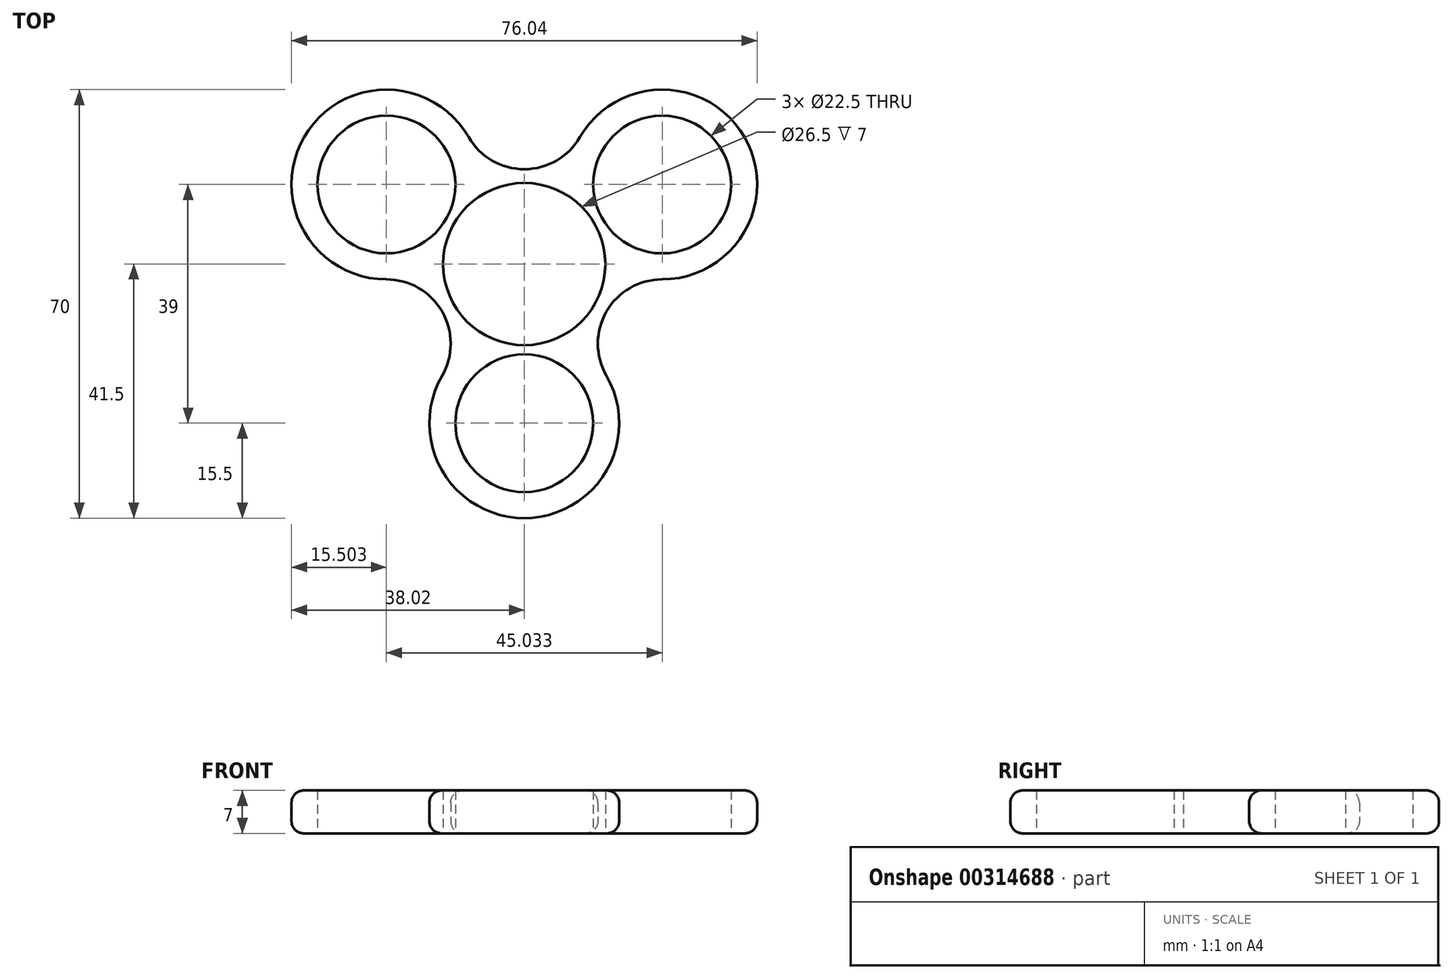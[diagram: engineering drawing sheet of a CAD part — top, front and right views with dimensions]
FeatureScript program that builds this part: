
annotation { "Feature Type Name" : "Feature", "Feature Type Description" : "" }
export const myFeature = defineFeature(function(context is Context, id is Id, definition is map)
    precondition{}
    {
        {
            var Q0;
            Q0=qCreatedBy(makeId("Top.planeOp"),FACE);
            var sketch = newSketch(context, id + "F0", { "sketchPlane" : qUnion([Q0])});
            skCircle(sketch, "E0", {"center": v(0, 0) * mm, "radius": 26 * mm, "construction": true});
            skCircle(sketch, "E1", {"center": v(0, 0) * mm, "radius": 13.25 * mm});
            skLineSegment(sketch, "E2", {"start": v(0, 35.35) * mm, "end": v(0, -50.13) * mm, "construction": true});
            skLineSegment(sketch, "E3", {"start": v(38.37, 22.15) * mm, "end": v(-45.13, -26.05) * mm, "construction": true});
            skLineSegment(sketch, "E4", {"start": v(-44.11, 25.47) * mm, "end": v(51.32, -29.63) * mm, "construction": true});
            skCircle(sketch, "E5", {"center": v(0, -26) * mm, "radius": 11.25 * mm});
            skCircle(sketch, "E6", {"center": v(-22.52, 13) * mm, "radius": 11.25 * mm});
            skCircle(sketch, "E7", {"center": v(22.52, 13) * mm, "radius": 11.25 * mm});
            skCircle(sketch, "E8", {"center": v(-22.52, 13) * mm, "radius": 15.5 * mm});
            skCircle(sketch, "E9", {"center": v(0, -26) * mm, "radius": 15.5 * mm});
            skCircle(sketch, "E10", {"center": v(22.52, 13) * mm, "radius": 15.5 * mm});
            skCircle(sketch, "E11", {"center": v(0, 26) * mm, "radius": 10.5 * mm});
            skCircle(sketch, "E12", {"center": v(22.52, -13) * mm, "radius": 10.5 * mm});
            skCircle(sketch, "E13", {"center": v(-22.52, -13) * mm, "radius": 10.5 * mm});
            skCircle(sketch, "E14", {"center": v(0, 0) * mm, "radius": 17.5 * mm});
            skCircle(sketch, "E15", {"center": v(0, 0) * mm, "radius": 41.5 * mm, "construction": true});
            skSolve(sketch);
        }
        {
            var Q0;
            Q0=makeQuery(id+"F0.imprint","IMPRINT",FACE,{"disambiguationData":[TD([[makeQuery(id+"F0.imprint","IMPRINT",EDGE,{"derivedFrom":sQuery(id+"F0.wireOp",EDGE,"E6")}),-1.0]])]});
            var Q1;
            {var subQ0=sQuery(id+"F0.wireOp",EDGE,"E13");var subQ1=sQuery(id+"F0.wireOp",EDGE,"E8");var subQ2=makeQuery(id+"F0.imprint","INTERSECT",VERTEX,{"derivedFrom":[subQ1,subQ0]});Q1=makeQuery(id+"F0.imprint","IMPRINT",FACE,{"disambiguationData":[TD([[makeQuery(id+"F0.imprint","IMPRINT",EDGE,{"disambiguationData":[TD([[subQ2,-1.0]])],"derivedFrom":subQ1}),-1.0]])]});}
            var Q2;
            {var subQ0=sQuery(id+"F0.wireOp",EDGE,"E11");var subQ1=sQuery(id+"F0.wireOp",EDGE,"E8");var subQ2=makeQuery(id+"F0.imprint","INTERSECT",VERTEX,{"derivedFrom":[subQ1,subQ0]});Q2=makeQuery(id+"F0.imprint","IMPRINT",FACE,{"disambiguationData":[TD([[makeQuery(id+"F0.imprint","IMPRINT",EDGE,{"disambiguationData":[TD([[subQ2,1.0]])],"derivedFrom":subQ1}),-1.0]])]});}
            var Q3;
            {var subQ0=sQuery(id+"F0.wireOp",EDGE,"E11");var subQ1=sQuery(id+"F0.wireOp",EDGE,"E10");var subQ2=makeQuery(id+"F0.imprint","INTERSECT",VERTEX,{"derivedFrom":[subQ1,subQ0]});Q3=makeQuery(id+"F0.imprint","IMPRINT",FACE,{"disambiguationData":[TD([[makeQuery(id+"F0.imprint","IMPRINT",EDGE,{"disambiguationData":[TD([[subQ2,-1.0]])],"derivedFrom":subQ1}),-1.0]])]});}
            var Q4;
            {var subQ0=sQuery(id+"F0.wireOp",EDGE,"E12");var subQ1=sQuery(id+"F0.wireOp",EDGE,"E10");var subQ2=makeQuery(id+"F0.imprint","INTERSECT",VERTEX,{"derivedFrom":[subQ1,subQ0]});Q4=makeQuery(id+"F0.imprint","IMPRINT",FACE,{"disambiguationData":[TD([[makeQuery(id+"F0.imprint","IMPRINT",EDGE,{"disambiguationData":[TD([[subQ2,1.0]])],"derivedFrom":subQ1}),-1.0]])]});}
            var Q5;
            Q5=makeQuery(id+"F0.imprint","IMPRINT",FACE,{"disambiguationData":[TD([[makeQuery(id+"F0.imprint","IMPRINT",EDGE,{"derivedFrom":sQuery(id+"F0.wireOp",EDGE,"E7")}),-1.0]])]});
            var Q6;
            {var subQ0=sQuery(id+"F0.wireOp",EDGE,"E12");var subQ1=sQuery(id+"F0.wireOp",EDGE,"E9");var subQ2=makeQuery(id+"F0.imprint","INTERSECT",VERTEX,{"derivedFrom":[subQ1,subQ0]});Q6=makeQuery(id+"F0.imprint","IMPRINT",FACE,{"disambiguationData":[TD([[makeQuery(id+"F0.imprint","IMPRINT",EDGE,{"disambiguationData":[TD([[subQ2,-1.0]])],"derivedFrom":subQ1}),-1.0]])]});}
            var Q7;
            Q7=makeQuery(id+"F0.imprint","IMPRINT",FACE,{"disambiguationData":[TD([[makeQuery(id+"F0.imprint","IMPRINT",EDGE,{"derivedFrom":sQuery(id+"F0.wireOp",EDGE,"E5")}),-1.0]])]});
            var Q8;
            {var subQ0=sQuery(id+"F0.wireOp",EDGE,"E13");var subQ1=sQuery(id+"F0.wireOp",EDGE,"E9");var subQ2=makeQuery(id+"F0.imprint","INTERSECT",VERTEX,{"derivedFrom":[subQ1,subQ0]});Q8=makeQuery(id+"F0.imprint","IMPRINT",FACE,{"disambiguationData":[TD([[makeQuery(id+"F0.imprint","IMPRINT",EDGE,{"disambiguationData":[TD([[subQ2,1.0]])],"derivedFrom":subQ1}),-1.0]])]});}
            var Q9;
            Q9=makeQuery(id+"F0.imprint","IMPRINT",FACE,{"disambiguationData":[TD([[makeQuery(id+"F0.imprint","IMPRINT",EDGE,{"derivedFrom":sQuery(id+"F0.wireOp",EDGE,"E1")}),-1.0]])]});
            var Q10;
            {var subQ0=sQuery(id+"F0.wireOp",EDGE,"E14");var subQ1=sQuery(id+"F0.wireOp",EDGE,"E9");var subQ2=makeQuery(id+"F0.imprint","INTERSECT",VERTEX,{"disambiguationData":[OD(0.0)],"derivedFrom":[subQ1,subQ0]});Q10=makeQuery(id+"F0.imprint","IMPRINT",FACE,{"disambiguationData":[TD([[makeQuery(id+"F0.imprint","IMPRINT",EDGE,{"disambiguationData":[TD([[subQ2,-1.0]])],"derivedFrom":subQ1}),1.0]])]});}
            var Q11;
            {var subQ0=sQuery(id+"F0.wireOp",EDGE,"E14");var subQ1=sQuery(id+"F0.wireOp",EDGE,"E8");var subQ2=makeQuery(id+"F0.imprint","INTERSECT",VERTEX,{"disambiguationData":[OD(0.0)],"derivedFrom":[subQ1,subQ0]});Q11=makeQuery(id+"F0.imprint","IMPRINT",FACE,{"disambiguationData":[TD([[makeQuery(id+"F0.imprint","IMPRINT",EDGE,{"disambiguationData":[TD([[subQ2,-1.0]])],"derivedFrom":subQ1}),1.0]])]});}
            var Q12;
            {var subQ0=sQuery(id+"F0.wireOp",EDGE,"E14");var subQ1=sQuery(id+"F0.wireOp",EDGE,"E10");var subQ2=makeQuery(id+"F0.imprint","INTERSECT",VERTEX,{"disambiguationData":[OD(0.0)],"derivedFrom":[subQ1,subQ0]});Q12=makeQuery(id+"F0.imprint","IMPRINT",FACE,{"disambiguationData":[TD([[makeQuery(id+"F0.imprint","IMPRINT",EDGE,{"disambiguationData":[TD([[subQ2,-1.0]])],"derivedFrom":subQ1}),1.0]])]});}
            extrude(context, id + "F1", {"entities" : qUnion([Q0, Q1, Q2, Q3, Q4, Q5, Q6, Q7, Q8, Q9, Q10, Q11, Q12]), "depth" : 3.5 * mm, "hasSecondDirection" : true, "secondDirectionOppositeDirection" : true, "secondDirectionDepth" : 3.5 * mm, "offsetDistance" : 25 * mm});
        }
        {
            var Q0;
            Q0=makeQuery(id+"F1.opExtrude","CAP_EDGE",EDGE,{"disambiguationData":[OSD([sQuery(id+"F0.wireOp",EDGE,"E8")])],"isStart":false});
            var Q1;
            Q1=makeQuery(id+"F1.opExtrude","CAP_EDGE",EDGE,{"disambiguationData":[OSD([sQuery(id+"F0.wireOp",EDGE,"E8")])],"isStart":true});
            fillet(context, id + "F2", {"entities" : qUnion([Q0, Q1]), "radius" : 2 * mm, "tangentPropagation" : true, "allowEdgeOverflow" : false});
        }
    });
